FCSTD DOCUMENT  (FreeCAD 0.20R27936 (Git))
Label: Voronoi_0_1
License: All rights reserved
LicenseURL: http://en.wikipedia.org/wiki/All_rights_reserved
objects: Sketcher::SketchObject×2, App::Part×1, Spreadsheet::Sheet×1
note: 2 computed .brp shape members not serialized (recipe doc carries the construction recipe); baked Part::Feature solids carry a one-line shape summary decoded from their .brp

FEATURE [App::Part] Part  label="Voronoi"
  Origin = -> Origin
FEATURE [Sketcher::SketchObject] Sketch  label="Triangle"
  FullyConstrained = false
  MapMode = 2
  Support = -> [Part]
  sketch-geometry (5):
    g0: LineSegment StartX=0 StartY=9.16828 StartZ=0 EndX=-8.18878 EndY=-21.3926 EndZ=0
    g1: LineSegment StartX=-8.18878 StartY=-21.3926 StartZ=0 EndX=8.18878 EndY=-21.3926 EndZ=0
    g2: LineSegment StartX=8.18878 StartY=-21.3926 StartZ=0 EndX=0 EndY=9.16828 EndZ=0
    g3: LineSegment StartX=0 StartY=9.16828 StartZ=0 EndX=0 EndY=-21.3926 EndZ=0
    g4: GeomPoint X=0 Y=0 Z=0
  constraints (14):
    c: Coincident(g0,g1)
    c: Horizontal(g1)
    c: Coincident(g1,g2)
    c: Coincident(g2,g0)
    c: Equal(g0,g2)
    c: Coincident(g3,g0)
    c: PointOnObject(g3,g1)
    c: Vertical(g3)
    c: PointOnObject(g4,g3)
    c: Angle(g0,g2) = 0.523599
    c: DistanceY(g0,g0) = 30.5609  'totHeight'
    c: DistanceY(g4,g0) = 9.16828
    c: Coincident(g4,g-1)
    c: DistanceX(g1,g1) = 16.3776  'totWidth'
FEATURE [Spreadsheet::Sheet] Spreadsheet  label="Values"
  cells = A1=Theta; B1(theta)==30°; A2=Mew; B2(mew)=0.3; A4=Max X; B4(maxX)==100cm; A5=Max Y; B5(maxY)==50cm; A7=Number of Points; B7(noPoints)=5
FEATURE [Sketcher::SketchObject] Sketch001  label="Layer1"
  FullyConstrained = true
